# Revit family: Electronics_Community-Point-Source_Biamp_Loudspeaker_R_2
name_source: partatom
category: Communication Devices
units: mm (PartAtom-declared; Revit-internal decimal feet)

## family parameters
Cut with Voids When Loaded = No
Host = Face
Maintain Annotation Orientation = No
OmniClass Number = 23.85.10.11.14.14.14
Part Type = Normal
Room Calculation Point = No
Round Connector Dimension = Use Diameter
Shared = No

## types (5) — shared parameters
Connector Description = Terminal strip; 400W 4 ohms (1600W peak) 40 V
Default Elevation = 48 "
Depth = 30.75 "
Description = R2 High Output Full-Range 60°X 60° Weather-Resistant Loudspeaker
Environmental = IP55 per IEC 60529, conforms with MIL-STD-810G
Finish = Refer to the Technical Drawing (page 3)
Grill Material = Biamp - Plastic - Gray(Grid)
Height = 24.76 "
Housing Material = Biamp - Plastic - Gray
Input Connection = 12' (3.6m) SJOW #16 cable
Manufacturer = Biamp
Mounting Points = (5) 3/8-16 threaded rigging points, Steel zinc-rich epoxy dual-layer powder-coated bracket; Aluminum aiming strap to secure angle
Operating Environment = Indoor /  Continuous outdoor direct exposure
Operating Mode = Passive
Product Documentation Link = https://downloads.biamp.com
Product Page URL = https://www.biamp.com
Product data url = https://www.bimobject.com
Recommended Amplifers = 400W - 800W @ 4 ohms,  (40V - 57V)
Transducers = LF 2 x 12 (305mm) weather-treated, Ferrofuid-cooledMF 2 x M200 2 exit, non-metallic diaphragm, Ferrofuid-cooled HF – 1 x 1 exit, titanium diaphragm
URL = https://www.biamp.com
Width = 24.76 "
Yoke Material = Biamp - Metal - Gray

## per-type parameters (varying)
| type | Equalized Maximum SPL | Equalized Sensitivity | Nominal Beamwidth  (H x V) | Nominal Maximum SPL (Whole Space) | Nominal Sensitivity | Operating Range | Weight |
| R2-52Z | Peak - 139dB; Continuous - 133dB | 1W - 107dB;2.83V - 110dB | 50° x  20° | Peak - 139dB; Continuous - 133dB | 1W - 107dB;2.83V - 110dB | 70 Hz to 16 kHz | 57.20 kgf |
| R2-77Z | Peak - 135dB; Continuous - 129dB | 1W - 103dB;2.83V - 106dB | 60° x  60° | Peak - 135dB; Continuous - 129dB | 1W - 103dB;2.83V - 106dB | 70 Hz to 16.5 kHz | 33.10 kgf |
| R2-94Z | Peak - 135dB; Continuous - 129dB | 1W - 103dB;2.83V - 106dB | 80° x  40° | Peak - 135dB; Continuous - 129dB | 1W - 103dB;2.83V - 106dB | 70 Hz to 15 kHz | 33.10 kgf |
| R2-474Z | Peak - 136dB; Continuous - 130dB | 1W - 104dB;2.83V - 107dB | 40°-70° x  40° | Peak - 136dB; Continuous - 130dB | 1W - 104dB;2.83V - 107dB | 70 Hz to 16 kHz | 33.10 kgf |
| R2-694Z | Peak - 136dB; Continuous - 130dB | 1W - 104dB;2.83V - 107dB | 60°-90° x  40° | Peak - 136dB; Continuous - 130dB | 1W - 104dB;2.83V - 107dB | 70 Hz to 16.5 kHz | 33.10 kgf |

note: column(s) folded — value = type name in every type: Model

## geometry (parser evidence)
native form markers: Sweep x4
no freeform markers — native parametric forms only
